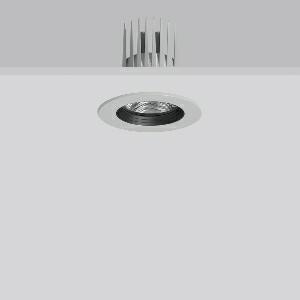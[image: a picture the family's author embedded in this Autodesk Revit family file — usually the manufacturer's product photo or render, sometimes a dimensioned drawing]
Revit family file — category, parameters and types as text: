
# Revit family: heledon_mini_e_901742_004_2414
name_source: partatom
category: Lighting Fixtures
units: mm (PartAtom-declared; Revit-internal decimal feet)

## family parameters
Cut with Voids When Loaded = No
Host = Face
Light Source = No
Part Type = Normal
Room Calculation Point = No
Round Connector Dimension = Use Diameter
Shared = No

## types (1)
- HELEDON mini E (1 x LED Modul 930, 2550 lm, 3000)
    Apparent Load = 20 VA
    Approval mark = CE
    CIE Flux Codes = 95 99 100 100 100
    Color Rendering = 90
    Color Temperature = 3000
    Default Elevation = 1800 mm
    Description = Series: HELEDON mini
Round recessed downlight. Housing: die-cast aluminium, powder-coated. Black plastic ring and recessed LED to prevent glare from the side. Optical assembly with reflector made of MIRO-Silver with 98% total light reflection for outstanding efficiency - can be changed without tools. Best colour rendering index Ra>90. Suitable for Recessed ceiling mounting. Installation without tools thanks to spring fastening system. Including separate LED converter with connecting cable 600 mm.High quality converter without flickering and stroboscopic effect. Through-wiring box (5 pole) available as accessory. The following accessories can be mounted without use of tools: interchangeable lenses, decorative glasses, honeycomb louvre, clear and frosted diffusers, white interchangeable plastic ring. 
Colour: silver
Diameter: 124 mm
Height: 3 mm
Cut-out diameter: 114 mm
Recess height: 170 mm
Luminaire: recess height: 120 mm
Lamp: LED
Socket: without socket
Colour temperature: 3000K
Colour rendering index (CRI): 92
System power: 20 W
Rated luminous flux: 2550 lm
Luminous efficiency: 128 lm/W
Control gear: Regulated power supply
Protection class: II
Type of protection: IP 20
    Height = 0 mm  [stored 0 ft]
    Lamp = 1 x LED Modul 930
    Lamp Light Flux = 2550 lm
    Lamp count = 1
    Length = 124 mm  [stored 0.406824 ft]
    Lifetime = 50000 h
    Luminous efficacy = 128 lm/W
    Manufacturer = RZB
    ModVariant = No
    Model = 901742.004
    Mounting Place = Ceiling
    Mounting Type = Recessed
    Number of Poles = 1
    OnlyDefault = Yes
    Power Factor = 1
    Product Name = HELEDON mini E
    Product group = Recessed downlights
    ProductGroupID = 402
    Protection Class = Protection class II
    Protection Degree = IP 20
    RLX_Detail_Level = 1
    RLX_Emergency_Light_Flux = 0 lm
    RLX_Emergency_Type = 0
    RLX_Emergency_Type_DB = No
    RlxData = <blob elided: 129201 chars, md5=ba0dd717>
    Socket = socket
    Standby Power = 0 W
    System Light Flux = 2550 lm
    System Power = 20 W
    Type Comments = Product without accessories
    Type Image = 901657.004.jpg
    URL = http://relux.com
    VarID = ---
    Voltage = 230 V
    Voltage Range = 220-240 V
    Weight = 0.00 kg
    Width = 0 mm  [stored 0 ft]

note: [stored X ft] marks values corroborated as IEEE doubles in the binary element streams (Revit-internal decimal feet)

## geometry (parser evidence)
native form markers: Blend x4, Sweep x10
no freeform markers — native parametric forms only
